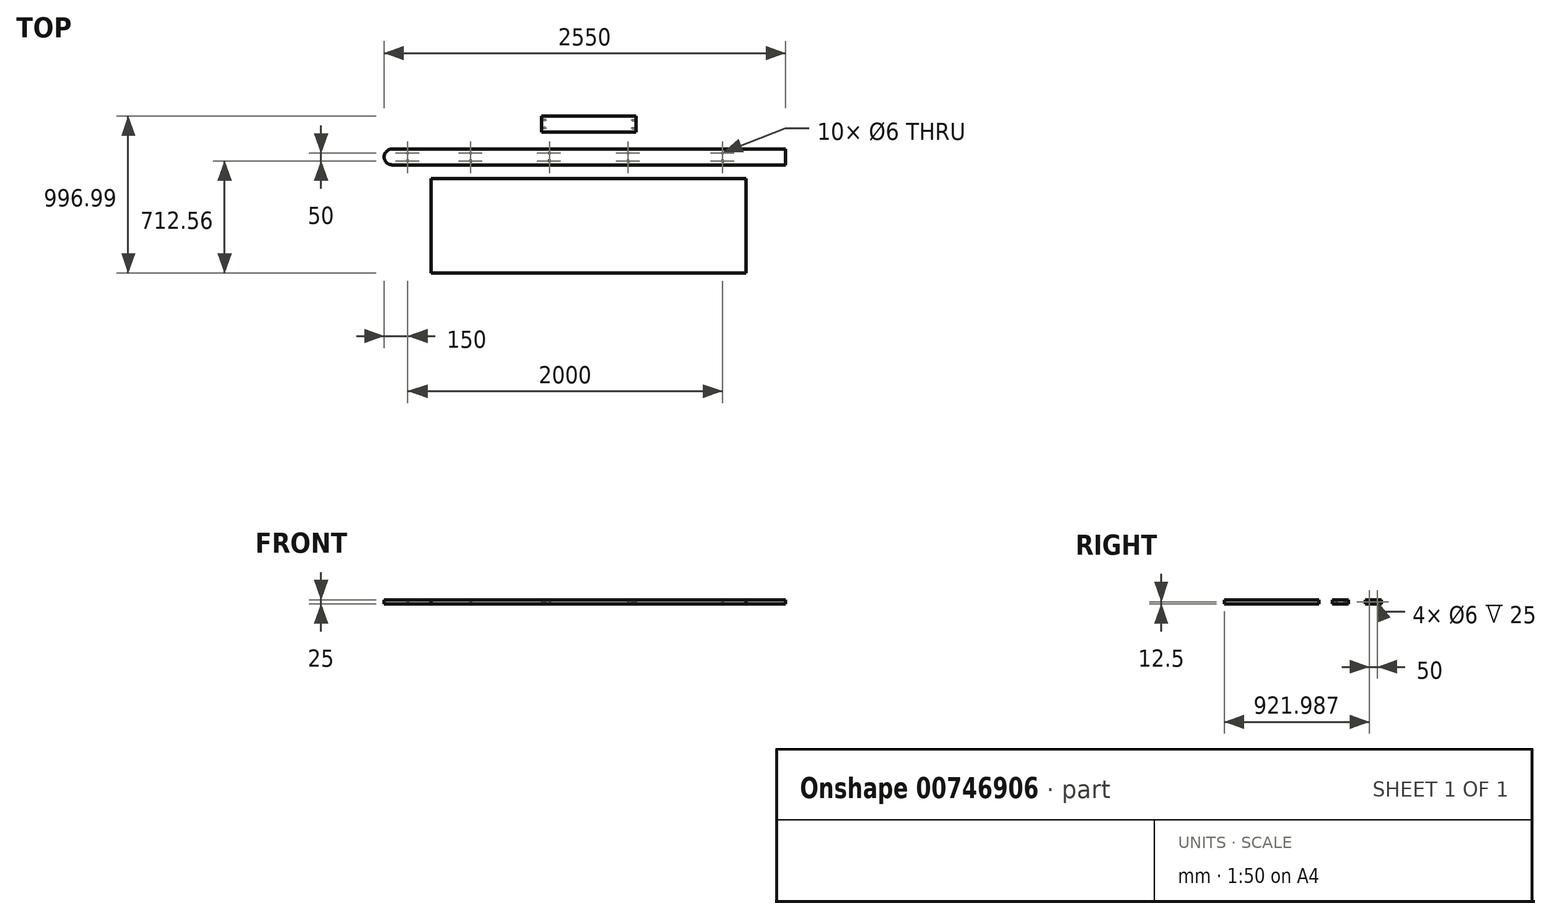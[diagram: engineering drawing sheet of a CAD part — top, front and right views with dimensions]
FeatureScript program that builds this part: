
annotation { "Feature Type Name" : "Feature", "Feature Type Description" : "" }
export const myFeature = defineFeature(function(context is Context, id is Id, definition is map)
    precondition{}
    {
        {
            var Q0;
            Q0=qCreatedBy(makeId("Top.planeOp"),FACE);
            var sketch = newSketch(context, id + "F0", { "sketchPlane" : qUnion([Q0])});
            skLineSegment(sketch, "E0.bottom", {"start": v(1250, -50) * mm, "end": v(-1250, -50) * mm});
            skLineSegment(sketch, "E0.top", {"start": v(1250, 50) * mm, "end": v(-1250, 50) * mm});
            skLineSegment(sketch, "E0.left", {"start": v(1250, -50) * mm, "end": v(1250, 50) * mm});
            skLineSegment(sketch, "E0.right", {"start": v(-1250, -50) * mm, "end": v(-1250, 50) * mm});
            skPoint(sketch, "E0.middle", {"position": v(0, 0) * mm});
            skArc(sketch, "E1", {"start": v(-1250, 50) * mm, "mid": v(-1300, 0) * mm, "end": v(-1250, -50) * mm});
            skCircle(sketch, "E2", {"center": v(850, 25) * mm, "radius": 3 * mm});
            skCircle(sketch, "E3", {"center": v(850, -25) * mm, "radius": 3 * mm});
            skLineSegment(sketch, "E4", {"start": v(1250, 0) * mm, "end": v(-1300, 0) * mm, "construction": true});
            skCircle(sketch, "E5", {"center": v(250, 25) * mm, "radius": 3 * mm});
            skCircle(sketch, "E6", {"center": v(250, -25) * mm, "radius": 3 * mm});
            skCircle(sketch, "E7", {"center": v(-250, 25) * mm, "radius": 3 * mm});
            skCircle(sketch, "E8", {"center": v(-250, -25) * mm, "radius": 3 * mm});
            skCircle(sketch, "E9", {"center": v(-750, 25) * mm, "radius": 3 * mm});
            skCircle(sketch, "E10", {"center": v(-750, -25) * mm, "radius": 3 * mm});
            skCircle(sketch, "E11", {"center": v(-1150, 25) * mm, "radius": 3 * mm});
            skCircle(sketch, "E12", {"center": v(-1150, -25) * mm, "radius": 3 * mm});
            skSolve(sketch);
        }
        {
            var Q0;
            Q0=makeQuery(id+"F0.imprint","IMPRINT",FACE,{"disambiguationData":[TD([[makeQuery(id+"F0.imprint","IMPRINT",EDGE,{"derivedFrom":sQuery(id+"F0.wireOp",EDGE,"E0.bottom")}),-1.0]])]});
            var Q1;
            Q1=makeQuery(id+"F0.imprint","IMPRINT",FACE,{"disambiguationData":[TD([[makeQuery(id+"F0.imprint","IMPRINT",EDGE,{"derivedFrom":sQuery(id+"F0.wireOp",EDGE,"E0.right")}),1.0]])]});
            extrude(context, id + "F1", {"entities" : qUnion([Q0, Q1]), "depth" : 25 * mm, "offsetDistance" : 25 * mm});
        }
        {
            var Q0;
            Q0=qCreatedBy(makeId("Top.planeOp"),FACE);
            var sketch = newSketch(context, id + "F2", { "sketchPlane" : qUnion([Q0])});
            skLineSegment(sketch, "E13.bottom", {"start": v(300, 159.43) * mm, "end": v(-300, 159.43) * mm});
            skLineSegment(sketch, "E13.top", {"start": v(300, 259.43) * mm, "end": v(-300, 259.43) * mm});
            skLineSegment(sketch, "E13.left", {"start": v(300, 159.43) * mm, "end": v(300, 259.43) * mm});
            skLineSegment(sketch, "E13.right", {"start": v(-300, 159.43) * mm, "end": v(-300, 259.43) * mm});
            skPoint(sketch, "E13.middle", {"position": v(0, 209.43) * mm});
            skSolve(sketch);
        }
        {
            var Q0;
            Q0=makeQuery(id+"F2.imprint","IMPRINT",FACE,{"disambiguationData":[TD([[makeQuery(id+"F2.imprint","IMPRINT",EDGE,{"derivedFrom":sQuery(id+"F2.wireOp",EDGE,"E13.bottom")}),-1.0]])]});
            extrude(context, id + "F3", {"entities" : qUnion([Q0]), "depth" : 25 * mm, "offsetDistance" : 25 * mm});
        }
        {
            var Q0;
            Q0=makeQuery(id+"F3.opExtrude","SWEPT_FACE",FACE,{"disambiguationData":[OSD([sQuery(id+"F2.wireOp",EDGE,"E13.right")])]});
            var sketch = newSketch(context, id + "F4", { "sketchPlane" : qUnion([Q0])});
            skSolve(sketch);
        }
        {
            var Q0;
            {var subQ0=sQuery(id+"F2.wireOp",EDGE,"E13.right");Q0=makeQuery(id+"F4.imprint","IMPRINT",FACE,{"disambiguationData":[TD([[makeQuery(id+"F4.imprint","IMPRINT",EDGE,{"derivedFrom":makeQuery(id+"F3.opExtrude","CAP_EDGE",EDGE,{"disambiguationData":[OSD([subQ0])],"isStart":true})}),-1.0]])]});}
            var sketch = newSketch(context, id + "F5", { "sketchPlane" : qUnion([Q0])});
            skCircle(sketch, "E14", {"center": v(-234.43, 12.5) * mm, "radius": 3 * mm});
            skCircle(sketch, "E15", {"center": v(-184.43, 12.5) * mm, "radius": 3 * mm});
            skLineSegment(sketch, "E16", {"start": v(-209.43, 0) * mm, "end": v(-209.43, 30.54) * mm, "construction": true});
            skSolve(sketch);
        }
        {
            var Q0;
            Q0=makeQuery(id+"F5.imprint","IMPRINT",FACE,{"disambiguationData":[TD([[makeQuery(id+"F5.imprint","IMPRINT",EDGE,{"derivedFrom":sQuery(id+"F5.wireOp",EDGE,"E14")}),1.0]])]});
            var Q1;
            Q1=makeQuery(id+"F5.imprint","IMPRINT",FACE,{"disambiguationData":[TD([[makeQuery(id+"F5.imprint","IMPRINT",EDGE,{"derivedFrom":sQuery(id+"F5.wireOp",EDGE,"E15")}),1.0]])]});
            extrude(context, id + "F6", {"entities" : qUnion([Q0, Q1]), "operationType" : NewBodyOperationType.REMOVE, "oppositeDirection" : true, "depth" : 25 * mm, "offsetDistance" : 25 * mm});
        }
        {
            var Q0;
            Q0=makeQuery(id+"F3.opExtrude","SWEPT_FACE",FACE,{"disambiguationData":[OSD([sQuery(id+"F2.wireOp",EDGE,"E13.left")])]});
            var sketch = newSketch(context, id + "F7", { "sketchPlane" : qUnion([Q0])});
            skPoint(sketch, "E17", {"position": v(259.43, 25) * mm});
            skPoint(sketch, "E18", {"position": v(259.43, 0) * mm});
            skPoint(sketch, "E19", {"position": v(159.43, 0) * mm});
            skPoint(sketch, "E20", {"position": v(159.43, 25) * mm});
            skLineSegment(sketch, "E21", {"start": v(209.43, 25) * mm, "end": v(209.43, 0) * mm, "construction": true});
            skLineSegment(sketch, "E22", {"start": v(259.43, 12.5) * mm, "end": v(159.43, 12.5) * mm, "construction": true});
            skCircle(sketch, "E23", {"center": v(184.43, 12.5) * mm, "radius": 3 * mm});
            skCircle(sketch, "E24", {"center": v(234.43, 12.5) * mm, "radius": 3 * mm});
            skSolve(sketch);
        }
        {
            var Q0;
            Q0 = qSketchRegion(id + "F7", true);
            extrude(context, id + "F8", {"entities" : qUnion([Q0]), "operationType" : NewBodyOperationType.REMOVE, "oppositeDirection" : true, "depth" : 25 * mm, "offsetDistance" : 25 * mm});
        }
        {
            var Q0;
            Q0=qCreatedBy(makeId("Top.planeOp"),FACE);
            var sketch = newSketch(context, id + "F9", { "sketchPlane" : qUnion([Q0])});
            skLineSegment(sketch, "E25.bottom", {"start": v(1000, -137.56) * mm, "end": v(-1000, -137.56) * mm});
            skLineSegment(sketch, "E25.top", {"start": v(1000, -737.56) * mm, "end": v(-1000, -737.56) * mm});
            skLineSegment(sketch, "E25.left", {"start": v(1000, -137.56) * mm, "end": v(1000, -737.56) * mm});
            skLineSegment(sketch, "E25.right", {"start": v(-1000, -137.56) * mm, "end": v(-1000, -737.56) * mm});
            skPoint(sketch, "E25.middle", {"position": v(0, -437.56) * mm});
            skSolve(sketch);
        }
        {
            var Q0;
            Q0=makeQuery(id+"F9.imprint","IMPRINT",FACE,{"disambiguationData":[TD([[makeQuery(id+"F9.imprint","IMPRINT",EDGE,{"derivedFrom":sQuery(id+"F9.wireOp",EDGE,"E25.bottom")}),1.0]])]});
            extrude(context, id + "F10", {"entities" : qUnion([Q0]), "depth" : 25 * mm, "offsetDistance" : 25 * mm});
        }
    });
